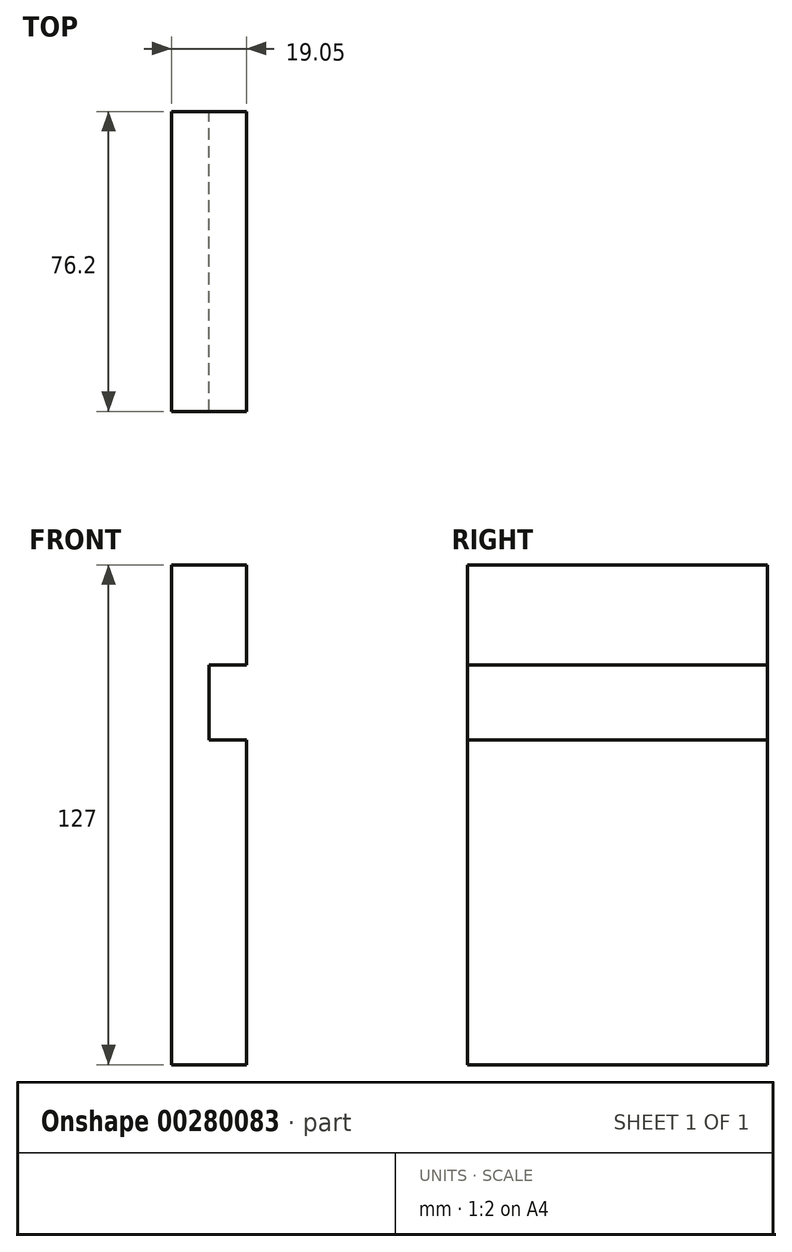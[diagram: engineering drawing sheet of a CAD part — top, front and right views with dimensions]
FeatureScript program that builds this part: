
annotation { "Feature Type Name" : "Feature", "Feature Type Description" : "" }
export const myFeature = defineFeature(function(context is Context, id is Id, definition is map)
    precondition{}
    {
        {
            var Q0;
            Q0=qCreatedBy(makeId("Front.planeOp"),FACE);
            var sketch = newSketch(context, id + "F0", { "sketchPlane" : qUnion([Q0])});
            skLineSegment(sketch, "E0", {"start": v(-76.2, 0) * mm, "end": v(-76.2, 127) * mm});
            skLineSegment(sketch, "E1", {"start": v(-76.2, 127) * mm, "end": v(-57.14, 127) * mm});
            skLineSegment(sketch, "E2", {"start": v(-57.14, 127) * mm, "end": v(-57.14, 101.6) * mm});
            skLineSegment(sketch, "E3", {"start": v(-57.14, 101.6) * mm, "end": v(-66.67, 101.6) * mm});
            skLineSegment(sketch, "E4", {"start": v(-66.67, 101.6) * mm, "end": v(-66.67, 82.55) * mm});
            skLineSegment(sketch, "E5", {"start": v(-66.67, 82.55) * mm, "end": v(-57.14, 82.55) * mm});
            skLineSegment(sketch, "E6", {"start": v(-57.14, 82.55) * mm, "end": v(-57.14, 0) * mm});
            skLineSegment(sketch, "E7", {"start": v(-57.14, 0) * mm, "end": v(-76.2, 0) * mm});
            skSolve(sketch);
        }
        {
            var Q0;
            Q0 = qSketchRegion(id + "F0", true);
            extrude(context, id + "F1", {"entities" : qUnion([Q0]), "depth" : 76.2 * mm});
        }
    });
